# Revit family: HOSPIVAC 2 SIRELLA
name_source: partatom
category: Equipement de génie climatique
revit_build: Autodesk Revit 2018 (Build: 20170223_1515(x64)
units: mm (PartAtom-declared; Revit-internal decimal feet)

## family parameters
Basée sur le plan de construction = Non
Classification = Aucun
Cote de connecteur circulaire = Utiliser le diamètre
Couper avec des vides une fois chargée = Non
Partagée = Non
Point de calcul de pièce = Non
Toujours verticalement = Oui
Type d'élément = Normal

## types (6) — shared parameters
ANGLE = 60.00°
COS_PHI = 0.9
DOUBLE_ALIMENTATION = Oui
ENTRAXE_ALIM_ELEC = 526 mm
ENTRAXE_CANA_ASPI = 900 mm
EP.VIROLE = 3 mm  [stored 0.00984252 ft]
FREQUENCE = 50 Hz
Fabricant = MIL'S
HAUT_ASPI = 60 mm  [stored 0.19685 ft]
HAUT_CANA_FILTRE = 30 mm  [stored 0.0984252 ft]
HAUT_REFOUL = 1520 mm
HAUT_TETE_FILTRE = 104 mm
HAUT_VIROLE = 155 mm  [stored 0.50853 ft]
LARGEUR = 1100 mm
LG_VIROLE = 2000 mm
LONGUEUR = 2400 mm
LONG_ENTRAXE_PIED = 1500 mm
LONG_FOND = 145 mm
LONG_OFFSET_REFOUL = 220 mm  [stored 0.721785 ft]
LONG_SELLETTE_1 = 1995 mm
Lien espace client = https://www.mils.fr
Modèle = HOSPIVAC
NBR_POLES = 3
NEUTRE = Oui
OFFSET2_LARG_ZONE_MAINT = 625 mm
OFFSET_CENTRAGE_PPE = 200 mm  [stored 0.656168 ft]
OFFSET_COUDE_CANA_FILTRE = 230 mm
OFFSET_HAUT_CANA_REFOUL = 820 mm
OFFSET_HAUT_FILTRE = 725 mm
OFFSET_HAUT_SELLETTE = 860 mm
OFFSET_LARG_ASPI_PPE = 150 mm
OFFSET_LARG_CANA_REFOUL = 294.5 mm
OFFSET_LARG_FILTRE = 410 mm
OFFSET_LARG_REFOUL = 503.5 mm
OFFSET_LONG_ASPI = 221 mm  [stored 0.725066 ft]
OFFSET_LONG_CANA_REFOUL = 1823 mm
OFFSET_LONG_FILTRE1 = 650 mm
OFFSET_LONG_FILTRE2 = 40 mm  [stored 0.131234 ft]
OFFSET_LONG_REFOUL = 945 mm
OFFSET_LONG_REFOUL_PPE_A = 945 mm
OFFSET_PPE = 40 mm  [stored 0.131234 ft]
OFFSET_SELLETTE_1 = 55 mm  [stored 0.180446 ft]
TENSION_ALIM = 400 V
TERRE = Oui
ØVIROLE = 650 mm

## per-type parameters (varying)
- c - HOSPIVAC 2 SL150.R: DEBIT_ASPI_VIDE=280.0 m³/h; DEBIT_REFOUL_VIDE=280.0 m³/h; DEGAG_CALORIFIQUE(kJ/h)=24805; DESCR_ALIM_X=Alimentation X ; 5G2.5mm²; DESCR_ALIM_Y=Alimentation Y ; 5G2.5mm²; DESCR_ASPI=Aspiration Vide ; 2x140 m³/h ; G 1"1/2 FEM; DESCR_REFOUL=Refoulement Vide ; 2x140 m³/h ; G 1"1/2"FEM; DIAM_ASPI_VIDE=50 mm  [stored 0.164042 ft]; DIAM_REFOUL_VIDE=40 mm  [stored 0.131234 ft]; HAUTEUR=1500 mm; HAUT_CANA_ASPI=1500 mm; HAUT_CANA_REFOUL=124 mm  [stored 0.406824 ft]; HAUT_FILTRE=380 mm; HAUT_FIX=15.2 mm; HAUT_REFOUL_PPE=949.8 mm; LONG_CANA_REFOUL=190.1 mm; LONG_REFOUL=65.2 mm  [stored 0.213911 ft]; LONG_U=650 mm; NIVEAU_SONORE(dB(A))=69; OFFSET1_LARG_ZONE_MAINT=697.5 mm; OFFSET_BRIDE=200 mm  [stored 0.656168 ft]; OFFSET_LARG_1=182 mm  [stored 0.597113 ft]; OFFSET_LARG_2=332 mm; OFFSET_LONG_A1=377 mm  [stored 1.23688 ft]; OFFSET_LONG_A2=637 mm; OFFSET_LONG_B1=1277 mm; OFFSET_LONG_B2=1537 mm; OFFSET_LONG_CANA_ASPI=597 mm; OFFSET_LONG_CANA_REFOUL_PPE_B=162.1 mm  [stored 0.531824 ft]; OFFSET_REFOUL_PPE_A=1001.1 mm; OFFSET_REFOUL_PPE_B=221.7 mm  [stored 0.727362 ft]; POIDS(Kg)=670 mm; PROTEC_ELECT_X=Disjoncteur courbe D - 10A; PROTEC_ELECT_Y=Disjoncteur courbe D - 10A; PUISS_APPARENTE_X=3333 VA; PUISS_APPARENTE_Y=3333 VA; PUISS_ELECT_X=3 kW; PUISS_ELECT_Y=3 kW; TAILLE_POMPE=SIRELLA SLR : SL150.R; TYPE_COFFRET=COFFRET ELEC STANDARD PM2 : COFFRET PM2 600x300x300; ØCANA=45 mm  [stored 0.147638 ft]; ØFILTRE=195 mm  [stored 0.639764 ft]; ØPOT_FILTRE=150 mm
- a - HOSPIVAC 2 SL100.R: DEBIT_ASPI_VIDE=180.0 m³/h; DEBIT_REFOUL_VIDE=180.0 m³/h; DEGAG_CALORIFIQUE(kJ/h)=18040; DESCR_ALIM_X=Alimentation X ; 5G2.5mm²; DESCR_ALIM_Y=Alimentation Y ; 5G2.5mm²; DESCR_ASPI=Aspiration Vide ; 2x90 m³/h ; G 1"1/4+ FEM; DESCR_REFOUL=Refoulement Vide ; 2x90 m³/h ; G 1"1/2 FEM; DIAM_ASPI_VIDE=32 mm  [stored 0.104987 ft]; DIAM_REFOUL_VIDE=40 mm  [stored 0.131234 ft]; HAUTEUR=1500 mm; HAUT_CANA_ASPI=1500 mm; HAUT_CANA_REFOUL=124 mm  [stored 0.406824 ft]; HAUT_FILTRE=425 mm; HAUT_FIX=15.2 mm; HAUT_REFOUL_PPE=949.8 mm; LONG_CANA_REFOUL=190.1 mm; LONG_REFOUL=65.2 mm  [stored 0.213911 ft]; LONG_U=650 mm; NIVEAU_SONORE(dB(A))=69; OFFSET1_LARG_ZONE_MAINT=656 mm; OFFSET_BRIDE=200.5 mm  [stored 0.657808 ft]; OFFSET_LARG_1=182 mm  [stored 0.597113 ft]; OFFSET_LARG_2=332 mm; OFFSET_LONG_A1=377 mm  [stored 1.23688 ft]; OFFSET_LONG_A2=637 mm; OFFSET_LONG_B1=1277 mm; OFFSET_LONG_B2=1537 mm; OFFSET_LONG_CANA_ASPI=597 mm; OFFSET_LONG_CANA_REFOUL_PPE_B=162.1 mm  [stored 0.531824 ft]; OFFSET_REFOUL_PPE_A=1001.1 mm; OFFSET_REFOUL_PPE_B=221.7 mm  [stored 0.727362 ft]; POIDS(Kg)=650 mm; PROTEC_ELECT_X=Disjoncteur courbe D - 10A; PROTEC_ELECT_Y=Disjoncteur courbe D - 10A; PUISS_APPARENTE_X=2444 VA; PUISS_APPARENTE_Y=2444 VA; PUISS_ELECT_X=2 kW; PUISS_ELECT_Y=2 kW; TAILLE_POMPE=SIRELLA SLR : SL100.R; TYPE_COFFRET=COFFRET ELEC STANDARD PM2 : COFFRET PM2 600x300x300; ØCANA=45 mm  [stored 0.147638 ft]; ØFILTRE=112 mm  [stored 0.367454 ft]; ØPOT_FILTRE=100 mm  [stored 0.328084 ft]
- e - HOSPIVAC 2 SL300.R: DEBIT_ASPI_VIDE=520.0 m³/h; DEBIT_REFOUL_VIDE=520.0 m³/h; DEGAG_CALORIFIQUE(kJ/h)=45144; DESCR_ALIM_X=Alimentation X ; 5G2.5mm²; DESCR_ALIM_Y=Alimentation Y ; 5G2.5mm²; DESCR_ASPI=Aspiration Vide ; 2x260 m³/h ; G 2"FEM; DESCR_REFOUL=Refoulement Vide ; 2x260 m³/h ; G 2"FEM; DIAM_ASPI_VIDE=50 mm  [stored 0.164042 ft]; DIAM_REFOUL_VIDE=50 mm  [stored 0.164042 ft]; HAUTEUR=1600 mm; HAUT_CANA_ASPI=1550 mm; HAUT_CANA_REFOUL=139 mm  [stored 0.456037 ft]; HAUT_FILTRE=380 mm; HAUT_FIX=24.4 mm  [stored 0.0800525 ft]; HAUT_REFOUL_PPE=950 mm; LONG_CANA_REFOUL=195 mm  [stored 0.639764 ft]; LONG_REFOUL=80 mm  [stored 0.262467 ft]; LONG_U=730 mm; NIVEAU_SONORE(dB(A))=70; OFFSET1_LARG_ZONE_MAINT=697.5 mm; OFFSET_BRIDE=266.5 mm; OFFSET_LARG_1=251 mm  [stored 0.823491 ft]; OFFSET_LARG_2=401 mm  [stored 1.31562 ft]; OFFSET_LONG_A1=337 mm  [stored 1.10564 ft]; OFFSET_LONG_A2=597 mm; OFFSET_LONG_B1=1237 mm; OFFSET_LONG_B2=1497 mm; OFFSET_LONG_CANA_ASPI=559 mm; OFFSET_LONG_CANA_REFOUL_PPE_B=192.6 mm  [stored 0.63189 ft]; OFFSET_REFOUL_PPE_A=974.7 mm; OFFSET_REFOUL_PPE_B=195.2 mm  [stored 0.64042 ft]; POIDS(Kg)=940 mm; PROTEC_ELECT_X=Disjoncteur courbe D - 20A; PROTEC_ELECT_Y=Disjoncteur courbe D - 20A; PUISS_APPARENTE_X=6111 VA; PUISS_APPARENTE_Y=6111 VA; PUISS_ELECT_X=6 kW; PUISS_ELECT_Y=6 kW; TAILLE_POMPE=SIRELLA SLR : SL300.R; TYPE_COFFRET=COFFRET ELEC STANDARD PM2 : COFFRET PM2 600x300x300; ØCANA=55 mm  [stored 0.180446 ft]; ØFILTRE=195 mm  [stored 0.639764 ft]; ØPOT_FILTRE=150 mm
- f - HOSPIVAC 2 RS SL300.R: DEBIT_ASPI_VIDE=572.0 m³/h; DEBIT_REFOUL_VIDE=572.0 m³/h; DEGAG_CALORIFIQUE(kJ/h)=62014; DESCR_ALIM_X=Alimentation X ; 5G4mm²; DESCR_ALIM_Y=Alimentation Y ; 5G4mm²; DESCR_ASPI=Aspiration Vide ; 572 m³/h ; G 2"FEM; DESCR_REFOUL=Refoulement Vide ; 572 m³/h ; G 2"FEM; DIAM_ASPI_VIDE=50 mm  [stored 0.164042 ft]; DIAM_REFOUL_VIDE=50 mm  [stored 0.164042 ft]; HAUTEUR=1700 mm; HAUT_CANA_ASPI=1550 mm; HAUT_CANA_REFOUL=139 mm  [stored 0.456037 ft]; HAUT_FILTRE=380 mm; HAUT_FIX=24.4 mm  [stored 0.0800525 ft]; HAUT_REFOUL_PPE=950 mm; LONG_CANA_REFOUL=195 mm  [stored 0.639764 ft]; LONG_REFOUL=80 mm  [stored 0.262467 ft]; LONG_U=730 mm; NIVEAU_SONORE(dB(A))=72; OFFSET1_LARG_ZONE_MAINT=697.5 mm; OFFSET_BRIDE=266.5 mm; OFFSET_LARG_1=251 mm  [stored 0.823491 ft]; OFFSET_LARG_2=401 mm  [stored 1.31562 ft]; OFFSET_LONG_A1=337 mm  [stored 1.10564 ft]; OFFSET_LONG_A2=597 mm; OFFSET_LONG_B1=1237 mm; OFFSET_LONG_B2=1497 mm; OFFSET_LONG_CANA_ASPI=559 mm; OFFSET_LONG_CANA_REFOUL_PPE_B=192.6 mm  [stored 0.63189 ft]; OFFSET_REFOUL_PPE_A=974.7 mm; OFFSET_REFOUL_PPE_B=195.2 mm  [stored 0.64042 ft]; POIDS(Kg)=990 mm; PROTEC_ELECT_X=Disjoncteur courbe D - 20A; PROTEC_ELECT_Y=Disjoncteur courbe D - 20A; PUISS_APPARENTE_X=8333 VA; PUISS_APPARENTE_Y=8333 VA; PUISS_ELECT_X=8 kW; PUISS_ELECT_Y=8 kW; TAILLE_POMPE=SIRELLA SLR : SL300.R; TYPE_COFFRET=COFFRET ELEC STANDARD PM2 : COFFRET PM2 600x800x300; ØCANA=55 mm  [stored 0.180446 ft]; ØFILTRE=195 mm  [stored 0.639764 ft]; ØPOT_FILTRE=150 mm
- b - HOSPIVAC 2 RS SL100.R: DEBIT_ASPI_VIDE=198.0 m³/h; DEBIT_REFOUL_VIDE=198.0 m³/h; DEGAG_CALORIFIQUE(kJ/h)=24805; DESCR_ALIM_X=Alimentation X ; 5G1.5mm²; DESCR_ALIM_Y=Alimentation Y ; 5G1.5mm²; DESCR_ASPI=Aspiration Vide ; 198 m³/h ; G 1"1/2FEM; DESCR_REFOUL=Refoulement Vide ; 198 m³/h ; G 1"1/2FEM; DIAM_ASPI_VIDE=40 mm  [stored 0.131234 ft]; DIAM_REFOUL_VIDE=40 mm  [stored 0.131234 ft]; HAUTEUR=1700 mm; HAUT_CANA_ASPI=1500 mm; HAUT_CANA_REFOUL=124 mm  [stored 0.406824 ft]; HAUT_FILTRE=425 mm; HAUT_FIX=15.2 mm; HAUT_REFOUL_PPE=949.8 mm; LONG_CANA_REFOUL=190.1 mm; LONG_REFOUL=65.2 mm  [stored 0.213911 ft]; LONG_U=650 mm; NIVEAU_SONORE(dB(A))=72; OFFSET1_LARG_ZONE_MAINT=656 mm; OFFSET_BRIDE=200.5 mm  [stored 0.657808 ft]; OFFSET_LARG_1=182 mm  [stored 0.597113 ft]; OFFSET_LARG_2=332 mm; OFFSET_LONG_A1=377 mm  [stored 1.23688 ft]; OFFSET_LONG_A2=637 mm; OFFSET_LONG_B1=1277 mm; OFFSET_LONG_B2=1537 mm; OFFSET_LONG_CANA_ASPI=597 mm; OFFSET_LONG_CANA_REFOUL_PPE_B=162.1 mm  [stored 0.531824 ft]; OFFSET_REFOUL_PPE_A=1001.1 mm; OFFSET_REFOUL_PPE_B=221.7 mm  [stored 0.727362 ft]; POIDS(Kg)=700 mm; PROTEC_ELECT_X=Disjoncteur courbe D - 10A; PROTEC_ELECT_Y=Disjoncteur courbe D - 10A; PUISS_APPARENTE_X=3333 VA; PUISS_APPARENTE_Y=3333 VA; PUISS_ELECT_X=3 kW; PUISS_ELECT_Y=3 kW; TAILLE_POMPE=SIRELLA SLR : SL100.R; TYPE_COFFRET=COFFRET ELEC STANDARD PM2 : COFFRET PM2 600x800x300; ØCANA=45 mm  [stored 0.147638 ft]; ØFILTRE=112 mm  [stored 0.367454 ft]; ØPOT_FILTRE=100 mm  [stored 0.328084 ft]
- d - HOSPIVAC 2 RS SL150.R: DEBIT_ASPI_VIDE=304.0 m³/h; DEBIT_REFOUL_VIDE=304.0 m³/h; DEGAG_CALORIFIQUE(kJ/h)=33074; DESCR_ALIM_X=Alimentation X ; 5G2.5mm²; DESCR_ALIM_Y=Alimentation Y ; 5G2.5mm²; DESCR_ASPI=Aspiration Vide ; 304 m³/h ; G 1"1/2 FEM; DESCR_REFOUL=Refoulement Vide ; 304 m³/h ; G 1"1/2 FEM; DIAM_ASPI_VIDE=40 mm  [stored 0.131234 ft]; DIAM_REFOUL_VIDE=40 mm  [stored 0.131234 ft]; HAUTEUR=1700 mm; HAUT_CANA_ASPI=1500 mm; HAUT_CANA_REFOUL=124 mm  [stored 0.406824 ft]; HAUT_FILTRE=380 mm; HAUT_FIX=15.2 mm; HAUT_REFOUL_PPE=949.8 mm; LONG_CANA_REFOUL=190.1 mm; LONG_REFOUL=65.2 mm  [stored 0.213911 ft]; LONG_U=650 mm; NIVEAU_SONORE(dB(A))=72; OFFSET1_LARG_ZONE_MAINT=697.5 mm; OFFSET_BRIDE=200 mm  [stored 0.656168 ft]; OFFSET_LARG_1=182 mm  [stored 0.597113 ft]; OFFSET_LARG_2=332 mm; OFFSET_LONG_A1=377 mm  [stored 1.23688 ft]; OFFSET_LONG_A2=637 mm; OFFSET_LONG_B1=1277 mm; OFFSET_LONG_B2=1537 mm; OFFSET_LONG_CANA_ASPI=597 mm; OFFSET_LONG_CANA_REFOUL_PPE_B=162.1 mm  [stored 0.531824 ft]; OFFSET_REFOUL_PPE_A=1001.1 mm; OFFSET_REFOUL_PPE_B=221.7 mm  [stored 0.727362 ft]; POIDS(Kg)=720 mm; PROTEC_ELECT_X=Disjoncteur courbe D - 10A; PROTEC_ELECT_Y=Disjoncteur courbe D - 10A; PUISS_APPARENTE_X=4444 VA; PUISS_APPARENTE_Y=4444 VA; PUISS_ELECT_X=4 kW; PUISS_ELECT_Y=4 kW; TAILLE_POMPE=SIRELLA SLR : SL150.R; TYPE_COFFRET=COFFRET ELEC STANDARD PM2 : COFFRET PM2 600x800x300; ØCANA=45 mm  [stored 0.147638 ft]; ØFILTRE=195 mm  [stored 0.639764 ft]; ØPOT_FILTRE=150 mm

note: [stored X ft] marks values corroborated as IEEE doubles in the binary element streams (Revit-internal decimal feet)
